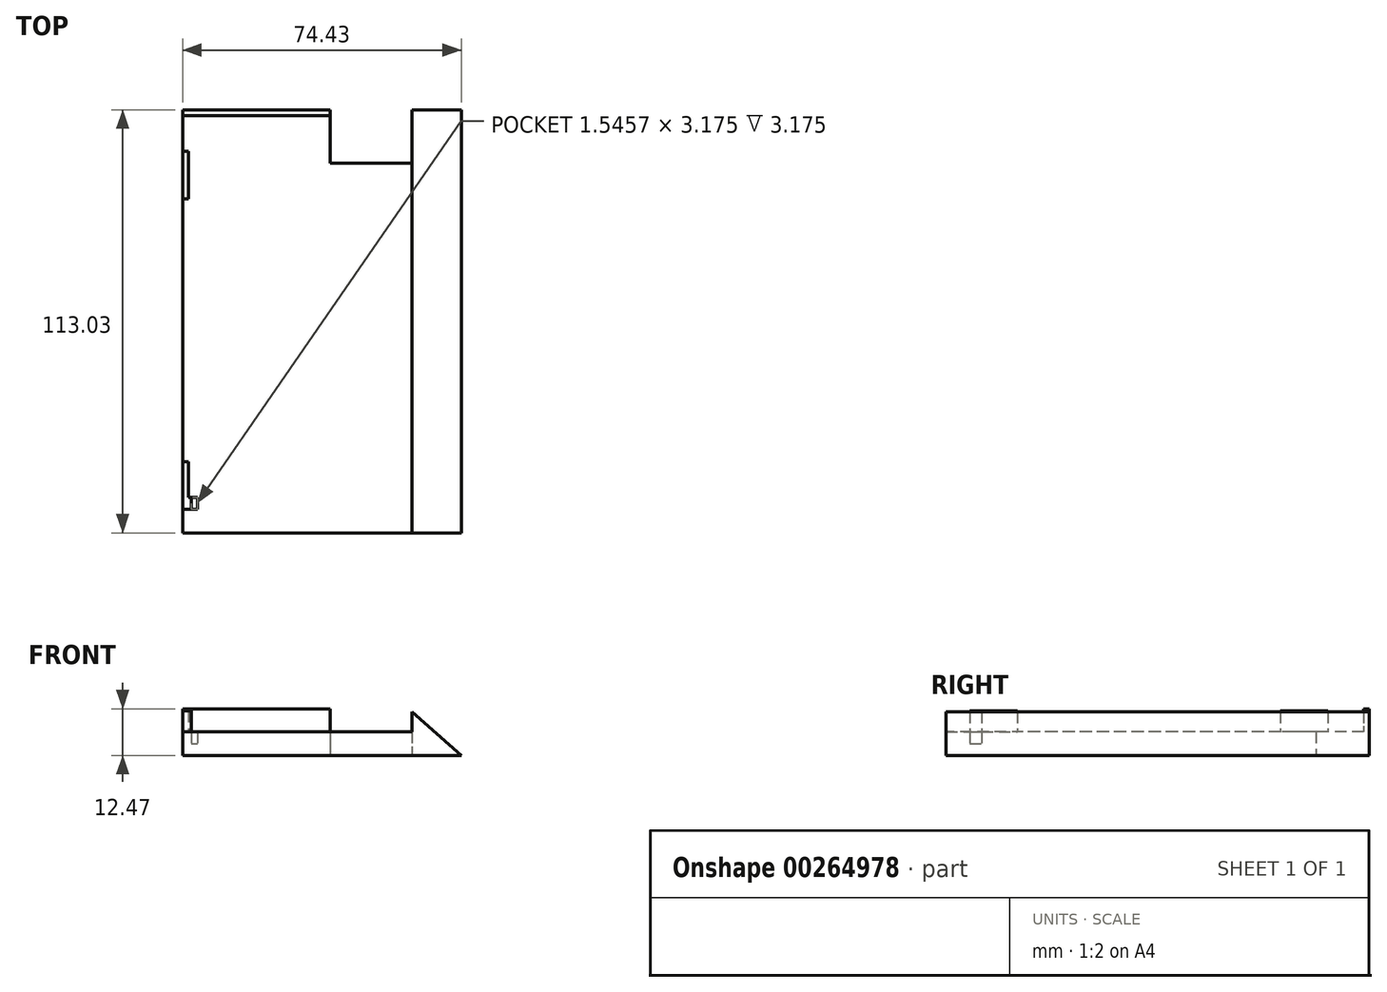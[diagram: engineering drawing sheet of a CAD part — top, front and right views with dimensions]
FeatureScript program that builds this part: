
annotation { "Feature Type Name" : "Feature", "Feature Type Description" : "" }
export const myFeature = defineFeature(function(context is Context, id is Id, definition is map)
    precondition{}
    {
        {
            var Q0;
            Q0=qCreatedBy(makeId("Top.planeOp"),FACE);
            var sketch = newSketch(context, id + "F0", { "sketchPlane" : qUnion([Q0])});
            skLineSegment(sketch, "E0.bottom", {"start": v(-36.5, 51.12) * mm, "end": v(2.98, 51.12) * mm});
            skLineSegment(sketch, "E0.top", {"start": v(-36.5, -61.91) * mm, "end": v(23.83, -61.91) * mm});
            skLineSegment(sketch, "E0.left", {"start": v(-36.5, 51.12) * mm, "end": v(-36.5, -6.67) * mm});
            skPoint(sketch, "E0.middle", {"position": v(0, -10.8) * mm});
            skLineSegment(sketch, "E1", {"start": v(-36.5, -61.91) * mm, "end": v(-34.91, -61.91) * mm});
            skLineSegment(sketch, "E2", {"start": v(-34.91, -61.91) * mm, "end": v(-34.91, -6.67) * mm});
            skLineSegment(sketch, "E3", {"start": v(-36.5, -61.91) * mm, "end": v(1.6, -61.91) * mm});
            skLineSegment(sketch, "E4", {"start": v(36.5, -61.91) * mm, "end": v(24.83, -61.91) * mm});
            skLineSegment(sketch, "E5", {"start": v(24.83, -52.15) * mm, "end": v(24.83, -61.91) * mm});
            skLineSegment(sketch, "E6", {"start": v(24.83, -52.15) * mm, "end": v(24.83, -6.67) * mm});
            skLineSegment(sketch, "E7", {"start": v(-36.5, 51.12) * mm, "end": v(-36.5, 49.53) * mm});
            skLineSegment(sketch, "E8", {"start": v(-36.5, 49.53) * mm, "end": v(2.98, 49.53) * mm});
            skLineSegment(sketch, "E9", {"start": v(2.98, 49.53) * mm, "end": v(2.98, 51.12) * mm});
            skLineSegment(sketch, "E10", {"start": v(2.98, 51.12) * mm, "end": v(2.98, 36.83) * mm});
            skLineSegment(sketch, "E11", {"start": v(2.98, 36.83) * mm, "end": v(24.03, 36.83) * mm});
            skLineSegment(sketch, "E12.trimOffspring", {"start": v(24.83, 51.12) * mm, "end": v(36.5, 51.12) * mm});
            skLineSegment(sketch, "E13", {"start": v(-36.5, -61.91) * mm, "end": v(-36.5, -55.56) * mm});
            skLineSegment(sketch, "E14", {"start": v(-36.5, -55.56) * mm, "end": v(-34.91, -55.56) * mm});
            skLineSegment(sketch, "E15", {"start": v(-36.5, -55.56) * mm, "end": v(-36.5, -52.39) * mm});
            skLineSegment(sketch, "E16", {"start": v(-36.5, -52.39) * mm, "end": v(-34.91, -52.39) * mm});
            skLineSegment(sketch, "E17", {"start": v(-34.91, -52.39) * mm, "end": v(-34.91, -55.56) * mm});
            skLineSegment(sketch, "E18", {"start": v(-36.5, -55.56) * mm, "end": v(-34.09, -55.56) * mm});
            skLineSegment(sketch, "E19", {"start": v(-34.09, -52.39) * mm, "end": v(-34.91, -52.39) * mm});
            skLineSegment(sketch, "E20", {"start": v(-36.5, 51.12) * mm, "end": v(-36.5, 40) * mm});
            skLineSegment(sketch, "E21", {"start": v(-36.5, 40) * mm, "end": v(-34.91, 40) * mm});
            skLineSegment(sketch, "E22", {"start": v(-34.91, 40) * mm, "end": v(-34.91, 36.83) * mm});
            skLineSegment(sketch, "E23", {"start": v(-34.94, 36.83) * mm, "end": v(-36.5, 36.83) * mm});
            skLineSegment(sketch, "E24", {"start": v(-36.5, 36.83) * mm, "end": v(-34.94, 36.83) * mm});
            skLineSegment(sketch, "E25", {"start": v(-33.97, 40) * mm, "end": v(-34.91, 40) * mm});
            skLineSegment(sketch, "E26.bottom", {"start": v(-36.5, -52.39) * mm, "end": v(-35.83, -52.39) * mm});
            skLineSegment(sketch, "E26.top", {"start": v(-35.83, -55.56) * mm, "end": v(-34.09, -55.56) * mm});
            skLineSegment(sketch, "E26.left", {"start": v(-35.83, -52.39) * mm, "end": v(-35.83, -55.56) * mm});
            skLineSegment(sketch, "E27.bottom", {"start": v(-35.72, 36.83) * mm, "end": v(-34.94, 36.83) * mm});
            skLineSegment(sketch, "E27.top", {"start": v(-35.72, 40) * mm, "end": v(-33.97, 40) * mm});
            skLineSegment(sketch, "E27.left", {"start": v(-35.72, 36.83) * mm, "end": v(-35.72, 40) * mm});
            skLineSegment(sketch, "E28.left", {"start": v(-35.83, -54.55) * mm, "end": v(-35.83, -53.37) * mm});
            skLineSegment(sketch, "E29.left", {"start": v(-35.72, 37.85) * mm, "end": v(-35.72, 38.9) * mm});
            skLineSegment(sketch, "E30", {"start": v(-34.09, -55.56) * mm, "end": v(-34.09, -52.39) * mm});
            skPoint(sketch, "E31.orphan", {"position": v(-32.54, -52.39) * mm});
            skPoint(sketch, "E32.start.orphan", {"position": v(-34.94, 36.83) * mm});
            skPoint(sketch, "E33.orphan", {"position": v(-32.54, 40) * mm});
            skPoint(sketch, "E34.orphan", {"position": v(23.83, 51.12) * mm});
            skLineSegment(sketch, "E35.trimOffspring", {"start": v(24.83, -61.91) * mm, "end": v(36.5, -61.91) * mm});
            skPoint(sketch, "E36.end.orphan", {"position": v(28.59, 51.12) * mm});
            skPoint(sketch, "E37.end.orphan", {"position": v(30.17, -61.91) * mm});
            skLineSegment(sketch, "E38", {"start": v(-34.09, -52.39) * mm, "end": v(-32.54, -52.39) * mm});
            skLineSegment(sketch, "E39", {"start": v(-32.54, -55.56) * mm, "end": v(-32.54, -52.39) * mm});
            skLineSegment(sketch, "E40", {"start": v(-32.54, -55.56) * mm, "end": v(-34.09, -55.56) * mm});
            skLineSegment(sketch, "E41", {"start": v(-34.91, 40) * mm, "end": v(-33.97, 40) * mm});
            skLineSegment(sketch, "E42", {"start": v(-34.91, 36.83) * mm, "end": v(-33.97, 36.83) * mm});
            skLineSegment(sketch, "E43", {"start": v(-34.91, 33.66) * mm, "end": v(-36.5, 33.66) * mm});
            skPoint(sketch, "E44.start.orphan", {"position": v(-32.54, 36.83) * mm});
            skLineSegment(sketch, "E45.MirrorCS", {"start": v(-36.5, -49.21) * mm, "end": v(-34.09, -49.21) * mm});
            skLineSegment(sketch, "E46.trimOffspring", {"start": v(-34.91, -52.39) * mm, "end": v(-34.09, -52.39) * mm});
            skLineSegment(sketch, "E47", {"start": v(24.03, 36.83) * mm, "end": v(24.83, 36.83) * mm});
            skLineSegment(sketch, "E48", {"start": v(24.57, 3.5) * mm, "end": v(24.83, 3.5) * mm});
            skLineSegment(sketch, "E49", {"start": v(24.57, -1.27) * mm, "end": v(24.83, -1.27) * mm});
            skLineSegment(sketch, "E50", {"start": v(24.57, -23.81) * mm, "end": v(24.83, -23.81) * mm});
            skLineSegment(sketch, "E51", {"start": v(24.57, -28.57) * mm, "end": v(24.83, -28.57) * mm});
            skLineSegment(sketch, "E52", {"start": v(23.83, -61.91) * mm, "end": v(24.83, -61.91) * mm});
            skPoint(sketch, "E53.end.orphan", {"position": v(39.05, 51.12) * mm});
            skLineSegment(sketch, "E54", {"start": v(-36.5, 33.66) * mm, "end": v(-36.5, 27.3) * mm});
            skLineSegment(sketch, "E55", {"start": v(-36.5, 27.3) * mm, "end": v(-34.91, 27.3) * mm});
            skLineSegment(sketch, "E56", {"start": v(-36.5, -49.21) * mm, "end": v(-36.5, -42.86) * mm});
            skLineSegment(sketch, "E57", {"start": v(-36.5, -42.86) * mm, "end": v(-34.91, -42.86) * mm});
            skLineSegment(sketch, "E58", {"start": v(36.5, -61.91) * mm, "end": v(37.93, -61.91) * mm});
            skLineSegment(sketch, "E59", {"start": v(37.93, -61.91) * mm, "end": v(37.93, -6.67) * mm});
            skLineSegment(sketch, "E60", {"start": v(37.93, 51.12) * mm, "end": v(36.5, 51.12) * mm});
            skLineSegment(sketch, "E61", {"start": v(36.5, -61.91) * mm, "end": v(36.5, -6.67) * mm});
            skLineSegment(sketch, "E62", {"start": v(36.5, 51.12) * mm, "end": v(36.5, -6.67) * mm});
            skLineSegment(sketch, "E63.trimOffspring", {"start": v(-36.5, -6.67) * mm, "end": v(-36.5, -61.91) * mm});
            skLineSegment(sketch, "E64.trimOffspring", {"start": v(-34.91, -6.67) * mm, "end": v(-34.91, 51.12) * mm});
            skLineSegment(sketch, "E65.trimOffspring", {"start": v(24.83, -6.67) * mm, "end": v(24.83, 51.12) * mm});
            skLineSegment(sketch, "E66.trimOffspring", {"start": v(36.5, -6.67) * mm, "end": v(36.5, -61.91) * mm});
            skLineSegment(sketch, "E67.trimOffspring", {"start": v(37.93, -6.67) * mm, "end": v(37.93, 51.12) * mm});
            skLineSegment(sketch, "E68.trimOffspring", {"start": v(36.5, -6.67) * mm, "end": v(36.5, 51.12) * mm});
            skSolve(sketch);
        }
        {
            var Q0;
            {var subQ12=sQuery(id+"F0.wireOp",EDGE,"E0.top");Q0=makeQuery(id+"F0.imprint","IMPRINT",FACE,{"disambiguationData":[TD([[makeQuery(id+"F0.imprint","IMPRINT",EDGE,{"derivedFrom":subQ12}),1.0]])]});}
            var Q1;
            {var subQ0=sQuery(id+"F0.wireOp",EDGE,"E17");Q1=makeQuery(id+"F0.imprint","IMPRINT",FACE,{"disambiguationData":[TD([[makeQuery(id+"F0.imprint","IMPRINT",EDGE,{"derivedFrom":subQ0}),1.0]])]});}
            var Q2;
            {var subQ0=sQuery(id+"F0.wireOp",EDGE,"E22");Q2=makeQuery(id+"F0.imprint","IMPRINT",FACE,{"disambiguationData":[TD([[makeQuery(id+"F0.imprint","IMPRINT",EDGE,{"derivedFrom":subQ0}),1.0]])]});}
            var Q3;
            Q3=makeQuery(id+"F0.imprint","IMPRINT",FACE,{"disambiguationData":[TD([[makeQuery(id+"F0.imprint","IMPRINT",EDGE,{"derivedFrom":sQuery(id+"F0.wireOp",EDGE,"E30")}),-1.0]])]});
            extrude(context, id + "F1", {"entities" : qUnion([Q0, Q1, Q2, Q3]), "depth" : 3.17 * mm});
        }
        {
            var Q0;
            {var subQ0=sQuery(id+"F0.wireOp",EDGE,"E10");var subQ1=sQuery(id+"F0.wireOp",EDGE,"E0.bottom");var subQ2=makeQuery(id+"F0.imprint","INTERSECT",VERTEX,{"derivedFrom":[subQ1,subQ0]});Q0=makeQuery(id+"F0.imprint","IMPRINT",FACE,{"disambiguationData":[TD([[makeQuery(id+"F0.imprint","IMPRINT",EDGE,{"disambiguationData":[TD([[subQ2,1.0]])],"derivedFrom":subQ1}),-1.0]])]});}
            var Q1;
            {var subQ0=sQuery(id+"F0.wireOp",EDGE,"E20");var subQ1=sQuery(id+"F0.wireOp",EDGE,"E0.bottom");var subQ2=makeQuery(id+"F0.imprint","INTERSECT",VERTEX,{"derivedFrom":[subQ1,subQ0]});Q1=makeQuery(id+"F0.imprint","IMPRINT",FACE,{"disambiguationData":[TD([[makeQuery(id+"F0.imprint","IMPRINT",EDGE,{"disambiguationData":[TD([[subQ2,-1.0]])],"derivedFrom":subQ1}),-1.0]])]});}
            extrude(context, id + "F2", {"entities" : qUnion([Q0, Q1]), "operationType" : NewBodyOperationType.ADD, "depth" : 12.47 * mm});
        }
        {
            var Q0;
            Q0=makeQuery(id+"F0.imprint","IMPRINT",FACE,{"disambiguationData":[TD([[makeQuery(id+"F0.imprint","IMPRINT",EDGE,{"derivedFrom":sQuery(id+"F0.wireOp",EDGE,"E30")}),-1.0]])]});
            extrude(context, id + "F3", {"entities" : qUnion([Q0]), "operationType" : NewBodyOperationType.REMOVE, "depth" : 12.7 * mm});
        }
        {
            var Q0;
            Q0=makeQuery(id+"F0.imprint","IMPRINT",FACE,{"disambiguationData":[TD([[makeQuery(id+"F0.imprint","IMPRINT",EDGE,{"derivedFrom":sQuery(id+"F0.wireOp",EDGE,"E30")}),-1.0]])]});
            extrude(context, id + "F4", {"entities" : qUnion([Q0]), "operationType" : NewBodyOperationType.ADD, "depth" : 3.17 * mm});
        }
        {
            var Q0;
            {var subQ2=sQuery(id+"F0.wireOp",EDGE,"E22");Q0=makeQuery(id+"F0.imprint","IMPRINT",FACE,{"disambiguationData":[TD([[makeQuery(id+"F0.imprint","IMPRINT",EDGE,{"derivedFrom":subQ2}),-1.0]])]});}
            var Q1;
            {var subQ0=sQuery(id+"F0.wireOp",EDGE,"E16");Q1=makeQuery(id+"F0.imprint","IMPRINT",FACE,{"disambiguationData":[TD([[makeQuery(id+"F0.imprint","IMPRINT",EDGE,{"derivedFrom":subQ0}),1.0]])]});}
            var Q2;
            {var subQ0=sQuery(id+"F0.wireOp",EDGE,"E15");Q2=makeQuery(id+"F0.imprint","IMPRINT",FACE,{"disambiguationData":[TD([[makeQuery(id+"F0.imprint","IMPRINT",EDGE,{"derivedFrom":subQ0}),-1.0]])]});}
            var Q3;
            {var subQ4=sQuery(id+"F0.wireOp",EDGE,"E16");Q3=makeQuery(id+"F0.imprint","IMPRINT",FACE,{"disambiguationData":[TD([[makeQuery(id+"F0.imprint","IMPRINT",EDGE,{"derivedFrom":subQ4}),-1.0]])]});}
            var Q4;
            {var subQ3=sQuery(id+"F0.wireOp",EDGE,"E21");Q4=makeQuery(id+"F0.imprint","IMPRINT",FACE,{"disambiguationData":[TD([[makeQuery(id+"F0.imprint","IMPRINT",EDGE,{"derivedFrom":subQ3}),-1.0]])]});}
            var Q5;
            {var subQ0=sQuery(id+"F0.wireOp",EDGE,"E43");Q5=makeQuery(id+"F0.imprint","IMPRINT",FACE,{"disambiguationData":[TD([[makeQuery(id+"F0.imprint","IMPRINT",EDGE,{"derivedFrom":subQ0}),1.0]])]});}
            var Q6;
            {var subQ4=sQuery(id+"F0.wireOp",EDGE,"E56");Q6=makeQuery(id+"F0.imprint","IMPRINT",FACE,{"disambiguationData":[TD([[makeQuery(id+"F0.imprint","IMPRINT",EDGE,{"derivedFrom":subQ4}),-1.0]])]});}
            var Q7;
            {var subQ1=sQuery(id+"F0.wireOp",EDGE,"E24");Q7=makeQuery(id+"F0.imprint","IMPRINT",FACE,{"disambiguationData":[TD([[makeQuery(id+"F0.imprint","IMPRINT",EDGE,{"derivedFrom":subQ1}),-1.0]])]});}
            var Q8;
            {var subQ0=sQuery(id+"F0.wireOp",EDGE,"E57");Q8=makeQuery(id+"F0.imprint","IMPRINT",FACE,{"disambiguationData":[TD([[makeQuery(id+"F0.imprint","IMPRINT",EDGE,{"derivedFrom":subQ0}),-1.0]])]});}
            var Q9;
            {var subQ1=sQuery(id+"F0.wireOp",EDGE,"E18");Q9=makeQuery(id+"F0.imprint","IMPRINT",FACE,{"disambiguationData":[TD([[makeQuery(id+"F0.imprint","IMPRINT",EDGE,{"derivedFrom":subQ1}),1.0]])]});}
            extrude(context, id + "F5", {"entities" : qUnion([Q0, Q1, Q2, Q3, Q4, Q5, Q6, Q7, Q8, Q9]), "operationType" : NewBodyOperationType.ADD, "depth" : 11.9 * mm});
        }
        {
            var Q0;
            {var subQ5=sQuery(id+"F0.wireOp",EDGE,"E5");Q0=makeQuery(id+"F0.imprint","IMPRINT",FACE,{"disambiguationData":[TD([[makeQuery(id+"F0.imprint","IMPRINT",EDGE,{"derivedFrom":subQ5}),1.0]])]});}
            var Q1;
            Q1=makeQuery(id+"F0.imprint","IMPRINT",FACE,{"disambiguationData":[TD([[makeQuery(id+"F0.imprint","IMPRINT",EDGE,{"derivedFrom":sQuery(id+"F0.wireOp",EDGE,"E58")}),1.0]])]});
            extrude(context, id + "F6", {"entities" : qUnion([Q0, Q1]), "operationType" : NewBodyOperationType.ADD, "depth" : 11.67 * mm});
        }
        {
            var Q0;
            {var subQ0=sQuery(id+"F0.wireOp",EDGE,"E21");Q0=makeQuery(id+"F0.imprint","IMPRINT",FACE,{"disambiguationData":[TD([[makeQuery(id+"F0.imprint","IMPRINT",EDGE,{"derivedFrom":subQ0}),1.0]])]});}
            var Q1;
            {var subQ0=sQuery(id+"F0.wireOp",EDGE,"E55");Q1=makeQuery(id+"F0.imprint","IMPRINT",FACE,{"disambiguationData":[TD([[makeQuery(id+"F0.imprint","IMPRINT",EDGE,{"derivedFrom":subQ0}),-1.0]])]});}
            var Q2;
            {var subQ1=sQuery(id+"F0.wireOp",EDGE,"E13");Q2=makeQuery(id+"F0.imprint","IMPRINT",FACE,{"disambiguationData":[TD([[makeQuery(id+"F0.imprint","IMPRINT",EDGE,{"derivedFrom":subQ1}),-1.0]])]});}
            var Q3;
            {var subQ0=sQuery(id+"F0.wireOp",EDGE,"E57");Q3=makeQuery(id+"F0.imprint","IMPRINT",FACE,{"disambiguationData":[TD([[makeQuery(id+"F0.imprint","IMPRINT",EDGE,{"derivedFrom":subQ0}),-1.0]])]});}
            var Q4;
            {var subQ0=sQuery(id+"F0.wireOp",EDGE,"E18");Q4=makeQuery(id+"F0.imprint","IMPRINT",FACE,{"disambiguationData":[TD([[makeQuery(id+"F0.imprint","IMPRINT",EDGE,{"derivedFrom":subQ0}),-1.0]])]});}
            extrude(context, id + "F7", {"entities" : qUnion([Q0, Q1, Q2, Q3, Q4]), "operationType" : NewBodyOperationType.ADD, "depth" : 6.35 * mm});
        }
        {
            var Q0;
            Q0=makeQuery(id+"F6.opExtrude","CAP_EDGE",EDGE,{"disambiguationData":[OSD([sQuery(id+"F0.wireOp",EDGE,"E59")])],"isStart":false});
            chamfer(context, id + "F8", {"entities" : qUnion([Q0]), "chamferType" : ChamferType.TWO_OFFSETS, "width1" : 13.1 * mm, "oppositeDirection" : false, "width2" : 11.67 * mm, "tangentPropagation" : true});
        }
    });
